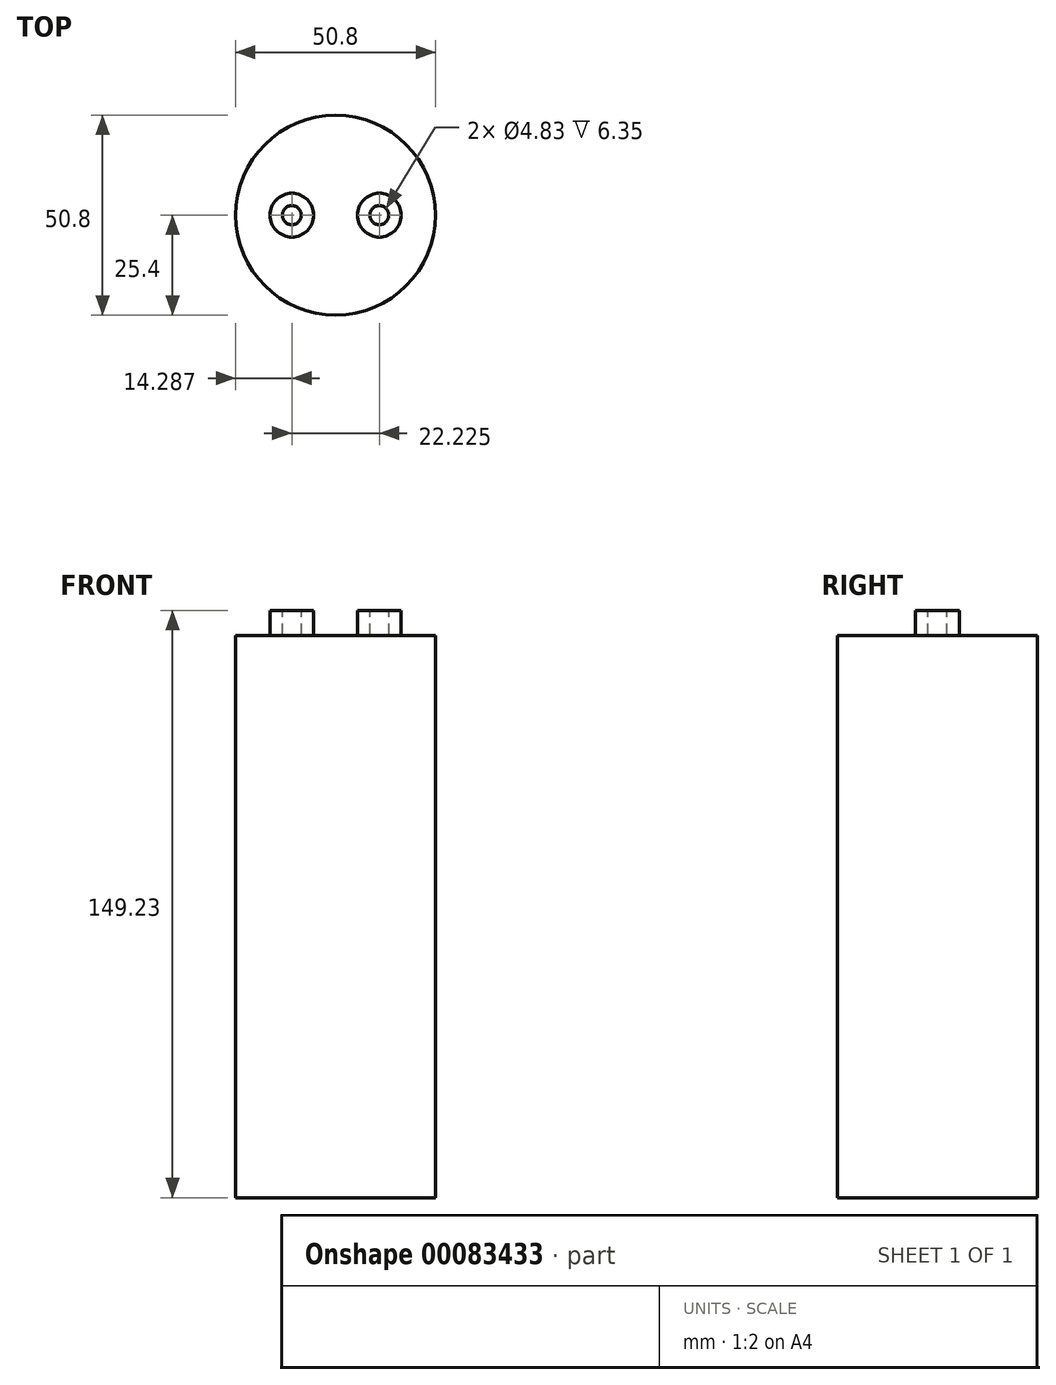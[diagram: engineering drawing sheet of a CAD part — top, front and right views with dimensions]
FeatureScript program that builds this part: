
annotation { "Feature Type Name" : "Feature", "Feature Type Description" : "" }
export const myFeature = defineFeature(function(context is Context, id is Id, definition is map)
    precondition{}
    {
        {
            var Q0;
            Q0=qCreatedBy(makeId("Top.planeOp"),FACE);
            var sketch = newSketch(context, id + "F0", { "sketchPlane" : qUnion([Q0])});
            skCircle(sketch, "E0", {"center": v(0, 0) * mm, "radius": 25.4 * mm});
            skSolve(sketch);
        }
        {
            var Q0;
            Q0 = qSketchRegion(id + "F0", true);
            extrude(context, id + "F1", {"entities" : qUnion([Q0]), "depth" : 142.88 * mm});
        }
        {
            var Q0;
            Q0=makeQuery(id+"F1.opExtrude","CAP_FACE",FACE,{"disambiguationData":[OSD([sQuery(id+"F0.wireOp",EDGE,"E0")])],"isStart":false});
            var sketch = newSketch(context, id + "F2", { "sketchPlane" : qUnion([Q0])});
            skLineSegment(sketch, "E1", {"start": v(-25.4, 0) * mm, "end": v(25.4, 0) * mm, "construction": true});
            skCircle(sketch, "E2", {"center": v(-11.11, 0) * mm, "radius": 5.56 * mm});
            skSolve(sketch);
        }
        {
            var Q0;
            Q0 = qSketchRegion(id + "F2", true);
            extrude(context, id + "F3", {"entities" : qUnion([Q0]), "operationType" : NewBodyOperationType.ADD, "depth" : 6.35 * mm});
        }
        {
            var Q0;
            Q0=makeQuery(id+"F3.opExtrude","CAP_FACE",FACE,{"disambiguationData":[OSD([sQuery(id+"F2.wireOp",EDGE,"E2")])],"isStart":false});
            var sketch = newSketch(context, id + "F4", { "sketchPlane" : qUnion([Q0])});
            skCircle(sketch, "E3", {"center": v(-11.11, 0) * mm, "radius": 2.41 * mm});
            skSolve(sketch);
        }
        {
            var Q0;
            Q0 = qSketchRegion(id + "F4", true);
            extrude(context, id + "F5", {"entities" : qUnion([Q0]), "operationType" : NewBodyOperationType.REMOVE, "oppositeDirection" : true, "depth" : 9.52 * mm});
        }
        {
            var Q0;
            Q0=makeQuery(id+"F1.opExtrude","SWEPT_BODY",BODY,{"disambiguationData":[OSD([sQuery(id+"F0.wireOp",EDGE,"E0")])]});
            var Q1;
            Q1=qCreatedBy(makeId("Right.planeOp"),FACE);
            mirror(context, id + "F6", {"operationType" : NewBodyOperationType.ADD, "entities" : qUnion([Q0]), "mirrorPlane" : qUnion([Q1])});
        }
    });
